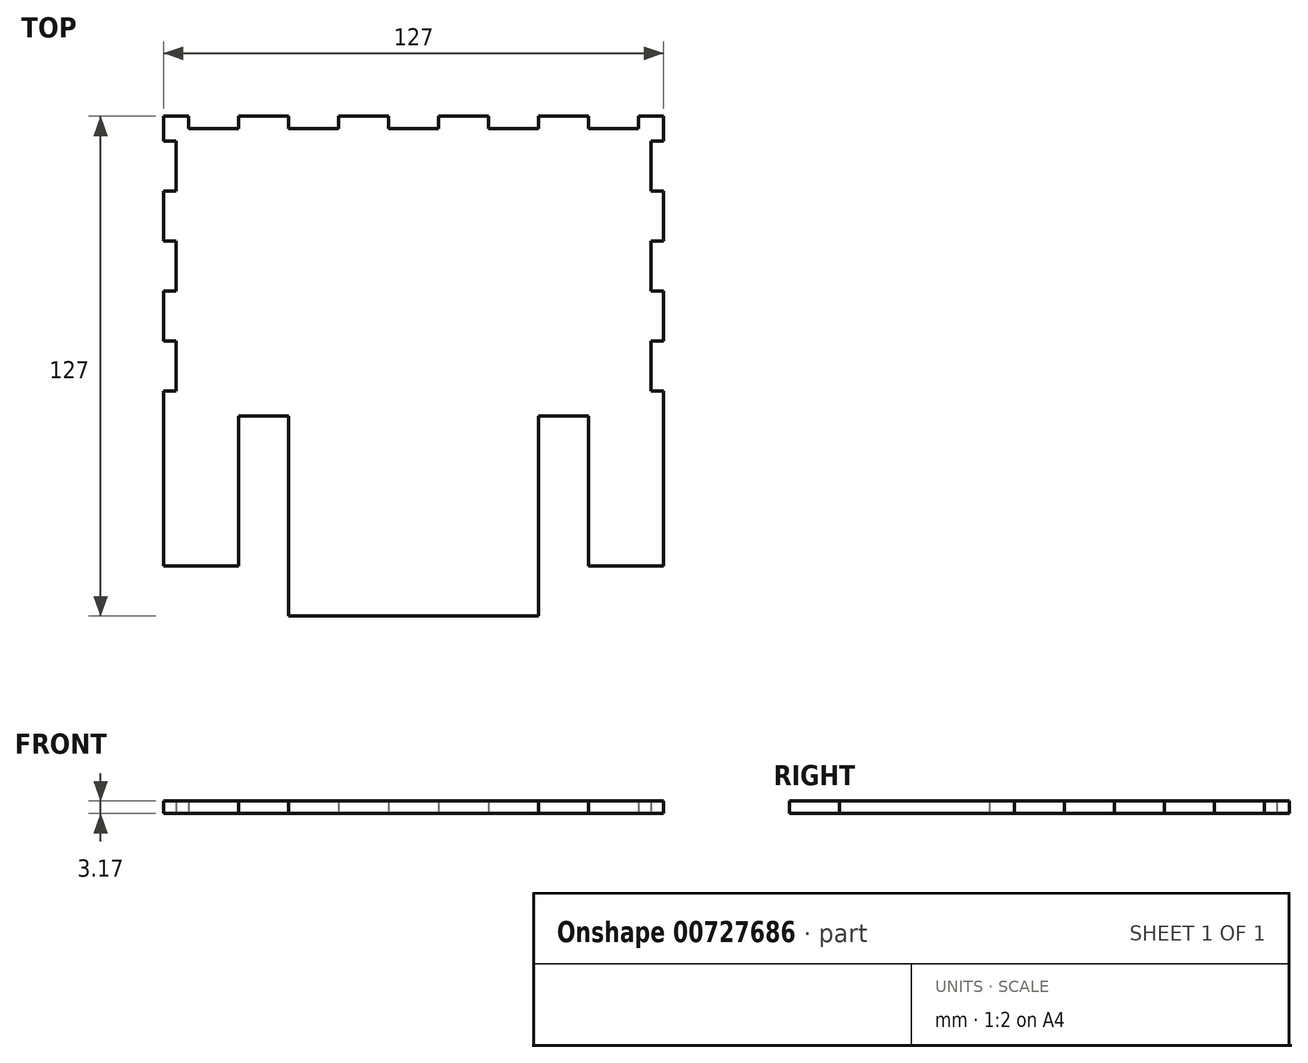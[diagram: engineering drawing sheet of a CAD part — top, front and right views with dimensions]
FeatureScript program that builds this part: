
annotation { "Feature Type Name" : "Feature", "Feature Type Description" : "" }
export const myFeature = defineFeature(function(context is Context, id is Id, definition is map)
    precondition{}
    {
        {
            var Q0;
            Q0=qCreatedBy(makeId("Top.planeOp"),FACE);
            var sketch = newSketch(context, id + "F0", { "sketchPlane" : qUnion([Q0])});
            skLineSegment(sketch, "E0.bottom", {"start": v(-88.05, 51.45) * mm, "end": v(38.95, 51.45) * mm});
            skLineSegment(sketch, "E0.top", {"start": v(-88.05, -24.75) * mm, "end": v(38.95, -24.75) * mm});
            skLineSegment(sketch, "E0.left", {"start": v(-88.05, 51.45) * mm, "end": v(-88.05, -24.75) * mm});
            skLineSegment(sketch, "E0.right", {"start": v(38.95, 51.45) * mm, "end": v(38.95, -24.75) * mm});
            skLineSegment(sketch, "E1", {"start": v(-24.55, -24.75) * mm, "end": v(-24.55, -75.55) * mm});
            skLineSegment(sketch, "E2", {"start": v(-24.55, -75.55) * mm, "end": v(-56.3, -75.55) * mm});
            skLineSegment(sketch, "E3", {"start": v(-56.3, -75.55) * mm, "end": v(-56.3, -24.75) * mm});
            skLineSegment(sketch, "E4", {"start": v(-24.55, -75.55) * mm, "end": v(7.2, -75.55) * mm});
            skLineSegment(sketch, "E5", {"start": v(7.2, -75.55) * mm, "end": v(7.2, -24.75) * mm});
            skLineSegment(sketch, "E6", {"start": v(-88.05, -24.75) * mm, "end": v(-88.05, -18.4) * mm});
            skLineSegment(sketch, "E7", {"start": v(-88.05, -18.4) * mm, "end": v(-84.87, -18.4) * mm});
            skLineSegment(sketch, "E8", {"start": v(-84.87, -18.4) * mm, "end": v(-84.87, 45.1) * mm});
            skLineSegment(sketch, "E9", {"start": v(-84.87, 45.1) * mm, "end": v(-88.05, 45.1) * mm});
            skLineSegment(sketch, "E10.MirrorCS", {"start": v(38.95, -18.4) * mm, "end": v(35.78, -18.4) * mm});
            skLineSegment(sketch, "E11.MirrorCS", {"start": v(35.78, -18.4) * mm, "end": v(35.78, 45.1) * mm});
            skLineSegment(sketch, "E12.MirrorCS", {"start": v(35.78, 45.1) * mm, "end": v(38.95, 45.1) * mm});
            skLineSegment(sketch, "E13", {"start": v(38.95, 51.45) * mm, "end": v(32.6, 51.45) * mm});
            skLineSegment(sketch, "E14", {"start": v(32.6, 51.45) * mm, "end": v(32.6, 48.28) * mm});
            skLineSegment(sketch, "E15", {"start": v(-84.87, 45.1) * mm, "end": v(-84.87, 32.4) * mm});
            skLineSegment(sketch, "E16", {"start": v(-84.87, 32.4) * mm, "end": v(-88.05, 32.4) * mm});
            skLineSegment(sketch, "E17", {"start": v(-88.05, 32.4) * mm, "end": v(-88.05, 19.7) * mm});
            skLineSegment(sketch, "E18", {"start": v(-88.05, 19.7) * mm, "end": v(-84.87, 19.7) * mm});
            skLineSegment(sketch, "E19", {"start": v(-84.87, 19.7) * mm, "end": v(-84.87, 7) * mm});
            skLineSegment(sketch, "E20", {"start": v(-84.87, 7) * mm, "end": v(-88.05, 7) * mm});
            skLineSegment(sketch, "E21", {"start": v(-88.05, 7) * mm, "end": v(-88.05, -5.7) * mm});
            skLineSegment(sketch, "E22", {"start": v(-88.05, -5.7) * mm, "end": v(-84.87, -5.7) * mm});
            skLineSegment(sketch, "E23.MirrorCS", {"start": v(38.95, -5.7) * mm, "end": v(35.78, -5.7) * mm});
            skLineSegment(sketch, "E24.MirrorCS", {"start": v(35.78, 7) * mm, "end": v(38.95, 7) * mm});
            skLineSegment(sketch, "E25.MirrorCS", {"start": v(38.95, 19.7) * mm, "end": v(35.78, 19.7) * mm});
            skLineSegment(sketch, "E26.MirrorCS", {"start": v(35.78, 32.4) * mm, "end": v(38.95, 32.4) * mm});
            skLineSegment(sketch, "E27", {"start": v(-81.7, 48.28) * mm, "end": v(-81.7, 51.45) * mm});
            skLineSegment(sketch, "E28", {"start": v(-81.7, 51.45) * mm, "end": v(-56.3, 51.45) * mm});
            skLineSegment(sketch, "E29", {"start": v(-56.3, 51.45) * mm, "end": v(-56.3, 48.28) * mm});
            skLineSegment(sketch, "E30", {"start": v(-56.3, 48.28) * mm, "end": v(-43.6, 48.28) * mm});
            skLineSegment(sketch, "E31", {"start": v(-43.6, 48.28) * mm, "end": v(-43.6, 51.45) * mm});
            skLineSegment(sketch, "E32", {"start": v(-43.6, 51.45) * mm, "end": v(-30.9, 51.45) * mm});
            skLineSegment(sketch, "E33", {"start": v(-30.9, 51.45) * mm, "end": v(-30.9, 48.28) * mm});
            skLineSegment(sketch, "E34", {"start": v(-30.9, 48.28) * mm, "end": v(-18.2, 48.28) * mm});
            skLineSegment(sketch, "E35", {"start": v(-18.2, 48.28) * mm, "end": v(-18.2, 51.45) * mm});
            skLineSegment(sketch, "E36", {"start": v(-18.2, 51.45) * mm, "end": v(7.2, 51.45) * mm});
            skLineSegment(sketch, "E37", {"start": v(-69, 51.45) * mm, "end": v(-69, 48.28) * mm});
            skLineSegment(sketch, "E38", {"start": v(-5.5, 51.45) * mm, "end": v(-5.5, 48.28) * mm});
            skLineSegment(sketch, "E39", {"start": v(32.6, 48.28) * mm, "end": v(19.9, 48.28) * mm});
            skLineSegment(sketch, "E40", {"start": v(-88.05, -24.75) * mm, "end": v(-88.05, -62.85) * mm});
            skLineSegment(sketch, "E41", {"start": v(-88.05, -62.85) * mm, "end": v(-69, -62.85) * mm});
            skLineSegment(sketch, "E42", {"start": v(-69, -62.85) * mm, "end": v(-69, -24.75) * mm});
            skLineSegment(sketch, "E43", {"start": v(38.95, -24.75) * mm, "end": v(38.95, -62.85) * mm});
            skLineSegment(sketch, "E44", {"start": v(38.95, -62.85) * mm, "end": v(19.9, -62.85) * mm});
            skLineSegment(sketch, "E45", {"start": v(19.9, -62.85) * mm, "end": v(19.9, -24.75) * mm});
            skLineSegment(sketch, "E46", {"start": v(7.2, 51.45) * mm, "end": v(7.2, 48.28) * mm});
            skLineSegment(sketch, "E47", {"start": v(19.9, 48.28) * mm, "end": v(19.9, 51.45) * mm});
            skLineSegment(sketch, "E48", {"start": v(19.9, 48.28) * mm, "end": v(-81.7, 48.28) * mm});
            skSolve(sketch);
        }
        {
            var Q0;
            {var subQ0=sQuery(id+"F0.wireOp",EDGE,"E1");Q0=makeQuery(id+"F0.imprint","IMPRINT",FACE,{"disambiguationData":[TD([[makeQuery(id+"F0.imprint","IMPRINT",EDGE,{"derivedFrom":subQ0}),1.0]])]});}
            var Q1;
            {var subQ0=sQuery(id+"F0.wireOp",EDGE,"E1");Q1=makeQuery(id+"F0.imprint","IMPRINT",FACE,{"disambiguationData":[TD([[makeQuery(id+"F0.imprint","IMPRINT",EDGE,{"derivedFrom":subQ0}),-1.0]])]});}
            var Q2;
            {var subQ10=sQuery(id+"F0.wireOp",EDGE,"E6");Q2=makeQuery(id+"F0.imprint","IMPRINT",FACE,{"disambiguationData":[TD([[makeQuery(id+"F0.imprint","IMPRINT",EDGE,{"derivedFrom":subQ10}),-1.0]])]});}
            var Q3;
            {var subQ0=sQuery(id+"F0.wireOp",EDGE,"E16");Q3=makeQuery(id+"F0.imprint","IMPRINT",FACE,{"disambiguationData":[TD([[makeQuery(id+"F0.imprint","IMPRINT",EDGE,{"derivedFrom":subQ0}),1.0]])]});}
            var Q4;
            {var subQ0=sQuery(id+"F0.wireOp",EDGE,"E20");Q4=makeQuery(id+"F0.imprint","IMPRINT",FACE,{"disambiguationData":[TD([[makeQuery(id+"F0.imprint","IMPRINT",EDGE,{"derivedFrom":subQ0}),1.0]])]});}
            var Q5;
            {var subQ0=sQuery(id+"F0.wireOp",EDGE,"E23.MirrorCS");Q5=makeQuery(id+"F0.imprint","IMPRINT",FACE,{"disambiguationData":[TD([[makeQuery(id+"F0.imprint","IMPRINT",EDGE,{"derivedFrom":subQ0}),-1.0]])]});}
            var Q6;
            {var subQ0=sQuery(id+"F0.wireOp",EDGE,"E25.MirrorCS");Q6=makeQuery(id+"F0.imprint","IMPRINT",FACE,{"disambiguationData":[TD([[makeQuery(id+"F0.imprint","IMPRINT",EDGE,{"derivedFrom":subQ0}),-1.0]])]});}
            var Q7;
            {var subQ0=sQuery(id+"F0.wireOp",EDGE,"E27");Q7=makeQuery(id+"F0.imprint","IMPRINT",FACE,{"disambiguationData":[TD([[makeQuery(id+"F0.imprint","IMPRINT",EDGE,{"derivedFrom":subQ0}),1.0]])]});}
            var Q8;
            {var subQ0=sQuery(id+"F0.wireOp",EDGE,"E29");Q8=makeQuery(id+"F0.imprint","IMPRINT",FACE,{"disambiguationData":[TD([[makeQuery(id+"F0.imprint","IMPRINT",EDGE,{"derivedFrom":subQ0}),-1.0]])]});}
            var Q9;
            {var subQ0=sQuery(id+"F0.wireOp",EDGE,"u6GVjwGg-xvUr-0UvW-mrOT-2NTPqF62j0Sp");Q9=makeQuery(id+"F0.imprint","IMPRINT",FACE,{"disambiguationData":[TD([[makeQuery(id+"F0.imprint","IMPRINT",EDGE,{"derivedFrom":subQ0}),1.0]])]});}
            var Q10;
            {var subQ0=sQuery(id+"F0.wireOp",EDGE,"E35");Q10=makeQuery(id+"F0.imprint","IMPRINT",FACE,{"disambiguationData":[TD([[makeQuery(id+"F0.imprint","IMPRINT",EDGE,{"derivedFrom":subQ0}),-1.0]])]});}
            var Q11;
            {var subQ0=sQuery(id+"F0.wireOp",EDGE,"E31");Q11=makeQuery(id+"F0.imprint","IMPRINT",FACE,{"disambiguationData":[TD([[makeQuery(id+"F0.imprint","IMPRINT",EDGE,{"derivedFrom":subQ0}),-1.0]])]});}
            var Q12;
            {var subQ0=sQuery(id+"F0.wireOp",EDGE,"E40");Q12=makeQuery(id+"F0.imprint","IMPRINT",FACE,{"disambiguationData":[TD([[makeQuery(id+"F0.imprint","IMPRINT",EDGE,{"derivedFrom":subQ0}),1.0]])]});}
            var Q13;
            {var subQ0=sQuery(id+"F0.wireOp",EDGE,"E43");Q13=makeQuery(id+"F0.imprint","IMPRINT",FACE,{"disambiguationData":[TD([[makeQuery(id+"F0.imprint","IMPRINT",EDGE,{"derivedFrom":subQ0}),-1.0]])]});}
            var Q14;
            {var subQ0=sQuery(id+"F0.wireOp",EDGE,"E46");Q14=makeQuery(id+"F0.imprint","IMPRINT",FACE,{"disambiguationData":[TD([[makeQuery(id+"F0.imprint","IMPRINT",EDGE,{"derivedFrom":subQ0}),1.0]])]});}
            extrude(context, id + "F1", {"entities" : qUnion([Q0, Q1, Q2, Q3, Q4, Q5, Q6, Q7, Q8, Q9, Q10, Q11, Q12, Q13, Q14]), "depth" : 3.17 * mm, "offsetDistance" : 25.4 * mm});
        }
    });
